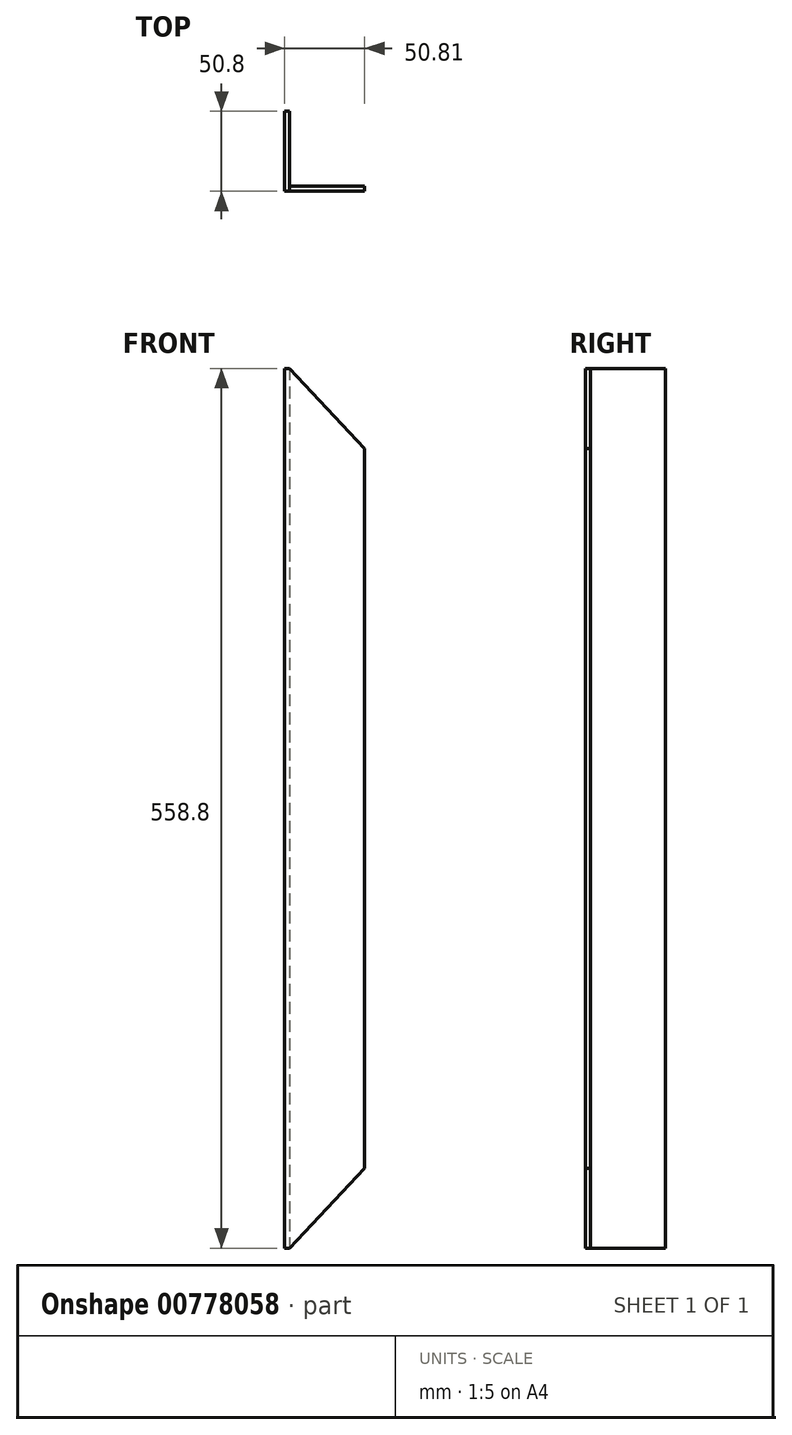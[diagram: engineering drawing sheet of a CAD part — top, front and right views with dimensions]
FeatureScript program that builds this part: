
annotation { "Feature Type Name" : "Feature", "Feature Type Description" : "" }
export const myFeature = defineFeature(function(context is Context, id is Id, definition is map)
    precondition{}
    {
        {
            var Q0;
            Q0=qCreatedBy(makeId("Top.planeOp"),FACE);
            var sketch = newSketch(context, id + "F0", { "sketchPlane" : qUnion([Q0])});
            skLineSegment(sketch, "E0", {"start": v(-3.17, 50.8) * mm, "end": v(-3.17, 0) * mm});
            skLineSegment(sketch, "E1", {"start": v(-3.17, 0) * mm, "end": v(47.62, 0) * mm});
            skLineSegment(sketch, "E2", {"start": v(47.63, 0) * mm, "end": v(47.63, 3.18) * mm});
            skLineSegment(sketch, "E3", {"start": v(47.63, 3.18) * mm, "end": v(0, 3.17) * mm});
            skLineSegment(sketch, "E4", {"start": v(0, 3.18) * mm, "end": v(0, 50.8) * mm});
            skLineSegment(sketch, "E5", {"start": v(0, 50.8) * mm, "end": v(-3.17, 50.8) * mm});
            skSolve(sketch);
        }
        {
            var Q0;
            Q0=makeQuery(id+"F0.imprint","IMPRINT",FACE,{"disambiguationData":[TD([[makeQuery(id+"F0.imprint","IMPRINT",EDGE,{"derivedFrom":sQuery(id+"F0.wireOp",EDGE,"E0")}),1.0]])]});
            extrude(context, id + "F1", {"entities" : qUnion([Q0]), "depth" : 533.4 * mm, "offsetDistance" : 25.4 * mm, "hasSecondDirection" : true, "secondDirectionOppositeDirection" : true, "secondDirectionDepth" : 25.4 * mm});
        }
        {
            var Q0;
            Q0=makeQuery(id+"F1.opExtrude","SWEPT_FACE",FACE,{"disambiguationData":[OSD([sQuery(id+"F0.wireOp",EDGE,"E3")])]});
            var sketch = newSketch(context, id + "F2", { "sketchPlane" : qUnion([Q0])});
            skLineSegment(sketch, "E6", {"start": v(-47.63, 25.4) * mm, "end": v(0, -25.4) * mm});
            skLineSegment(sketch, "E7", {"start": v(-47.63, 482.6) * mm, "end": v(0, 533.4) * mm});
            skSolve(sketch);
        }
        {
            var Q0;
            {var subQ0=sQuery(id+"F2.wireOp",EDGE,"E7");Q0=makeQuery(id+"F2.imprint","IMPRINT",FACE,{"disambiguationData":[TD([[makeQuery(id+"F2.imprint","IMPRINT",EDGE,{"derivedFrom":subQ0}),1.0]])]});}
            var Q1;
            {var subQ0=sQuery(id+"F2.wireOp",EDGE,"E6");Q1=makeQuery(id+"F2.imprint","IMPRINT",FACE,{"disambiguationData":[TD([[makeQuery(id+"F2.imprint","IMPRINT",EDGE,{"derivedFrom":subQ0}),-1.0]])]});}
            extrude(context, id + "F3", {"entities" : qUnion([Q0, Q1]), "operationType" : NewBodyOperationType.REMOVE, "endBound" : BoundingType.THROUGH_ALL, "oppositeDirection" : true, "depth" : 25.4 * mm, "offsetDistance" : 25.4 * mm});
        }
    });
